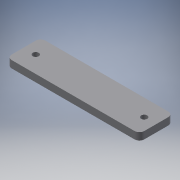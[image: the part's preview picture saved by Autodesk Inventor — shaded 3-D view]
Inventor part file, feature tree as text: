
AUTODESK INVENTOR PART (.ipt)
format: ipt  version: 2018 (Build 220112000, 112)  size: 144,896 bytes
history: native  units: mm
features: other x6, reference x5, extrude x1, fillet x1, sketch x1
ambient origin geometry x8: Origin, YZ Plane, XZ Plane, XY Plane, X Axis, Y Axis, Z Axis, Center Point
bodies: Solid1 (feature_tree)
feature tree (14):
  extrude  "Extrusion1"  Depth=14.0mm
  fillet  "Fillet1"  Radius=3.0mm
  sketch  "Sketch1"  dims[d0=7.0mm d1=14.0mm d2=3.0mm d3=0.0mm d4=2.0mm]
  reference  "Reference1"
  reference  "Reference2"
  reference  "Reference3"
  reference  "Reference4"
  reference  "Reference5"
  other  "<userpath>\OneDrive\Documents\Inventor\TSA\2018\Animatronics\Tortoise\TurtleAssembly.iam"
  other  "TurtleAssembly.iam"
  other  "Frame - Copy:1"
  other  "HeadAssembly:1"
  other  "HeadBottom:1"
  other  "HeadBase:1"
